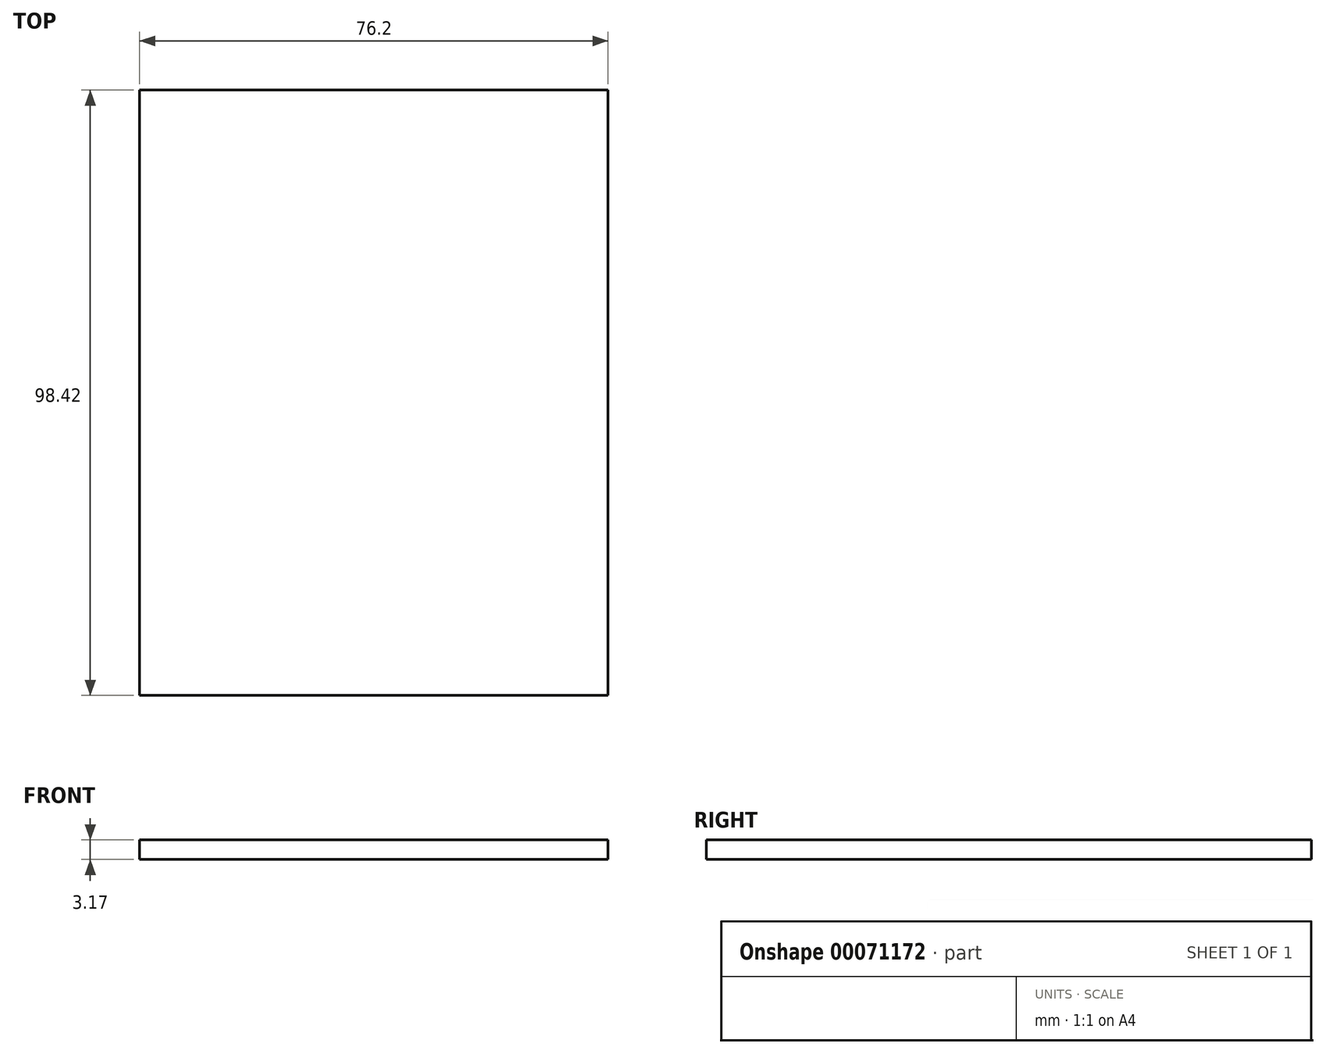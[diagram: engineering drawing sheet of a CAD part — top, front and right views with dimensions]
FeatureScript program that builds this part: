
annotation { "Feature Type Name" : "Feature", "Feature Type Description" : "" }
export const myFeature = defineFeature(function(context is Context, id is Id, definition is map)
    precondition{}
    {
        {
            var Q0;
            Q0=qCreatedBy(makeId("Top.planeOp"),FACE);
            var sketch = newSketch(context, id + "F0", { "sketchPlane" : qUnion([Q0])});
            skLineSegment(sketch, "E0.rect.bottom", {"start": v(38.1, 49.21) * mm, "end": v(-38.1, 49.21) * mm});
            skLineSegment(sketch, "E0.rect.top", {"start": v(38.1, -49.21) * mm, "end": v(-38.1, -49.21) * mm});
            skLineSegment(sketch, "E0.rect.left", {"start": v(38.1, 49.21) * mm, "end": v(38.1, -49.21) * mm});
            skLineSegment(sketch, "E0.rect.right", {"start": v(-38.1, 49.21) * mm, "end": v(-38.1, -49.21) * mm});
            skPoint(sketch, "E0.rect.middle", {"position": v(0, 0) * mm});
            skSolve(sketch);
        }
        {
            var Q0;
            Q0=makeQuery(id+"F0.imprint","IMPRINT",FACE,{"disambiguationData":[TD([[makeQuery(id+"F0.imprint","IMPRINT",EDGE,{"derivedFrom":sQuery(id+"F0.wireOp",EDGE,"E0.rect.bottom")}),1.0]])]});
            extrude(context, id + "F1", {"entities" : qUnion([Q0]), "depth" : 3.17 * mm});
        }
    });
